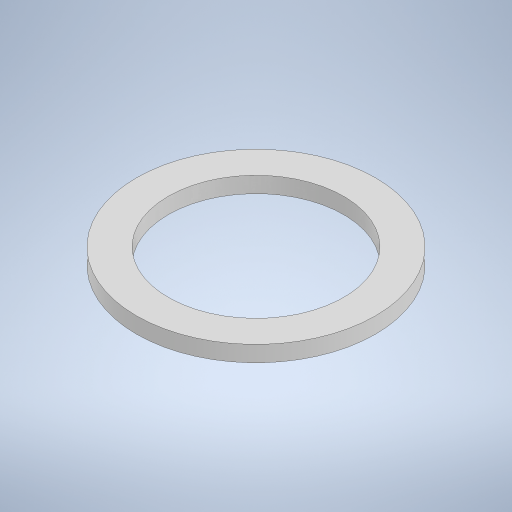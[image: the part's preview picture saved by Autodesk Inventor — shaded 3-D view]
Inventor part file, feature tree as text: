
AUTODESK INVENTOR PART (.ipt)
format: ipt  version: 2024.1 (Build 281209000, 209)  size: 228,864 bytes
history: native  units: mm
features: other x1, extrude x1, sketch x1
ambient origin geometry x8: Origin, YZ Plane, XZ Plane, XY Plane, X Axis, Y Axis, Z Axis, Center Point
bodies: Body1 (feature_tree)
feature tree (3):
  other  "ソリッド1"
  extrude  "押し出し1"  Depth=22.0mm
  sketch  "スケッチ1"
